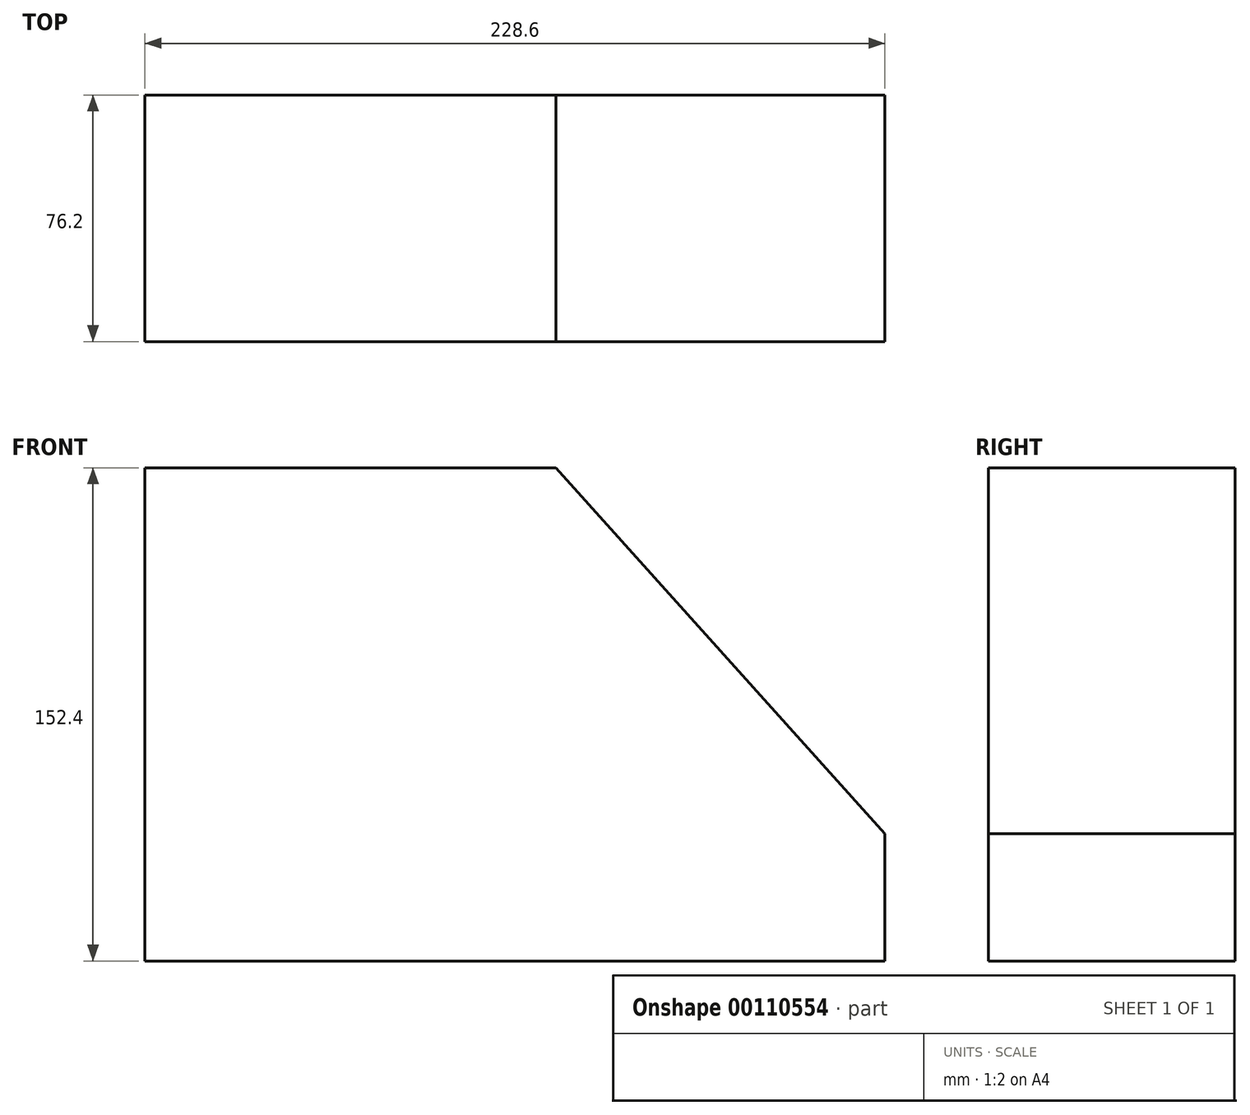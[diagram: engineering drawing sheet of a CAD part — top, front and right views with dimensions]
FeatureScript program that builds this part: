
annotation { "Feature Type Name" : "Feature", "Feature Type Description" : "" }
export const myFeature = defineFeature(function(context is Context, id is Id, definition is map)
    precondition{}
    {
        {
            var Q0;
            Q0=qCreatedBy(makeId("Front.planeOp"),FACE);
            var sketch = newSketch(context, id + "F0", { "sketchPlane" : qUnion([Q0])});
            skLineSegment(sketch, "E0", {"start": v(-107.2, 72.21) * mm, "end": v(19.8, 72.21) * mm});
            skLineSegment(sketch, "E1", {"start": v(19.8, 72.21) * mm, "end": v(121.4, -40.83) * mm});
            skLineSegment(sketch, "E2", {"start": v(121.4, -40.83) * mm, "end": v(121.4, -80.19) * mm});
            skLineSegment(sketch, "E3", {"start": v(121.4, -80.19) * mm, "end": v(-107.2, -80.19) * mm});
            skLineSegment(sketch, "E4", {"start": v(-107.2, -80.19) * mm, "end": v(-107.2, 72.21) * mm});
            skSolve(sketch);
        }
        {
            var Q0;
            Q0 = qSketchRegion(id + "F0", true);
            extrude(context, id + "F1", {"entities" : qUnion([Q0]), "depth" : 76.2 * mm});
        }
    });
